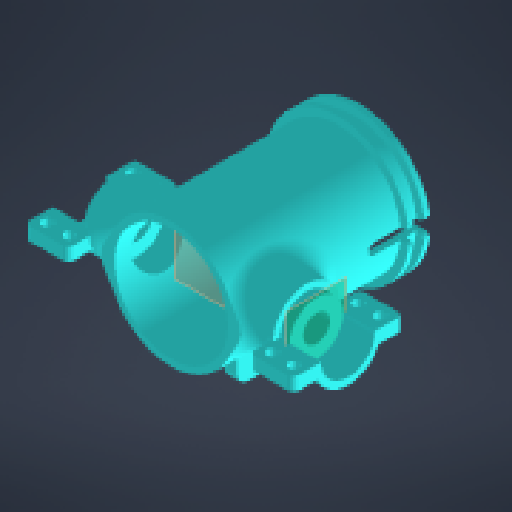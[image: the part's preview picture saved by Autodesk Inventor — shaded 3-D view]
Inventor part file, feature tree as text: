
AUTODESK INVENTOR PART (.ipt)
format: ipt  version: 2024 (Build 280153000, 153)  size: 611,328 bytes
history: native  units: mm
features: sketch x12, other x11, extrude x10, fillet x6, mirror x3, revolve x2, reference x1
ambient origin geometry x8: Origin, YZ Plane, XZ Plane, XY Plane, X Axis, Y Axis, Z Axis, Center Point
bodies: Body1 (feature_tree)
feature tree (45):
  other  "Твердое тело1"
  extrude  "Выдавливание1"  Depth=70.0mm TaperAngle=0.0deg
  other  "РабПлоскость2"
  revolve  "Вращение1"
  fillet  "Сопряжение1"  Radius=42.0mm
  extrude  "Выдавливание2"  Depth=47.0mm
  extrude  "Выдавливание3"  [1 undecoded]
  extrude  "Выдавливание4"  Depth=100.0mm
  fillet  "Сопряжение2"  Radius=25.0mm
  extrude  "Выдавливание5"  TaperAngle=90.0deg  [1 undecoded]
  revolve  "Вращение2"
  fillet  "Сопряжение3"  Radius=10.0mm
  extrude  "Выдавливание6"  Depth=20.0mm
  fillet  "Сопряжение4"  [1 undecoded]
  fillet  "Сопряжение5"  Radius=12.0mm
  other  "РабПлоскость4"
  extrude  "Выдавливание8"  Depth=5.0mm
  extrude  "Выдавливание11"  Depth=7.5mm
  extrude  "Выдавливание12"  Depth=40.0mm TaperAngle=0.0deg
  fillet  "Сопряжение6"  Radius=3.0mm
  mirror  "Зеркальное отражение5"
  mirror  "Зеркальное отражение6"
  other  "РабПлоскость6"
  extrude  "Выдавливание13"  Depth=5.0mm
  mirror  "Зеркальное отражение7"
  sketch  "Эскиз1"
  reference  "Ссылка1"
  sketch  "Эскиз3"
  sketch  "Эскиз4"
  sketch  "Эскиз5"
  sketch  "Эскиз6"
  sketch  "Эскиз7"
  sketch  "Эскиз8"
  sketch  "Эскиз9"
  sketch  "Эскиз11"
  sketch  "Эскиз14"
  sketch  "Эскиз15"
  sketch  "Эскиз16"
  parser-record x2  (decoder bookkeeping rows leaked as tree rows — omitted from the tree; the rows remain in map.json)
  other  "motor_assembly_M.iam"
  other  "motor:1"
  other  "default_motor_asembly.iam"
  other  "bushing_assembly:1"
  other  "bushing:1"
note: 3 required parameter values undecoded (feature->parameter linkage not recoverable at this tier; creation-order binding heuristic only, values carry confidence <= 0.55)
note: 2 file-system paths scrubbed to <path> (originals preserved in map.json)
